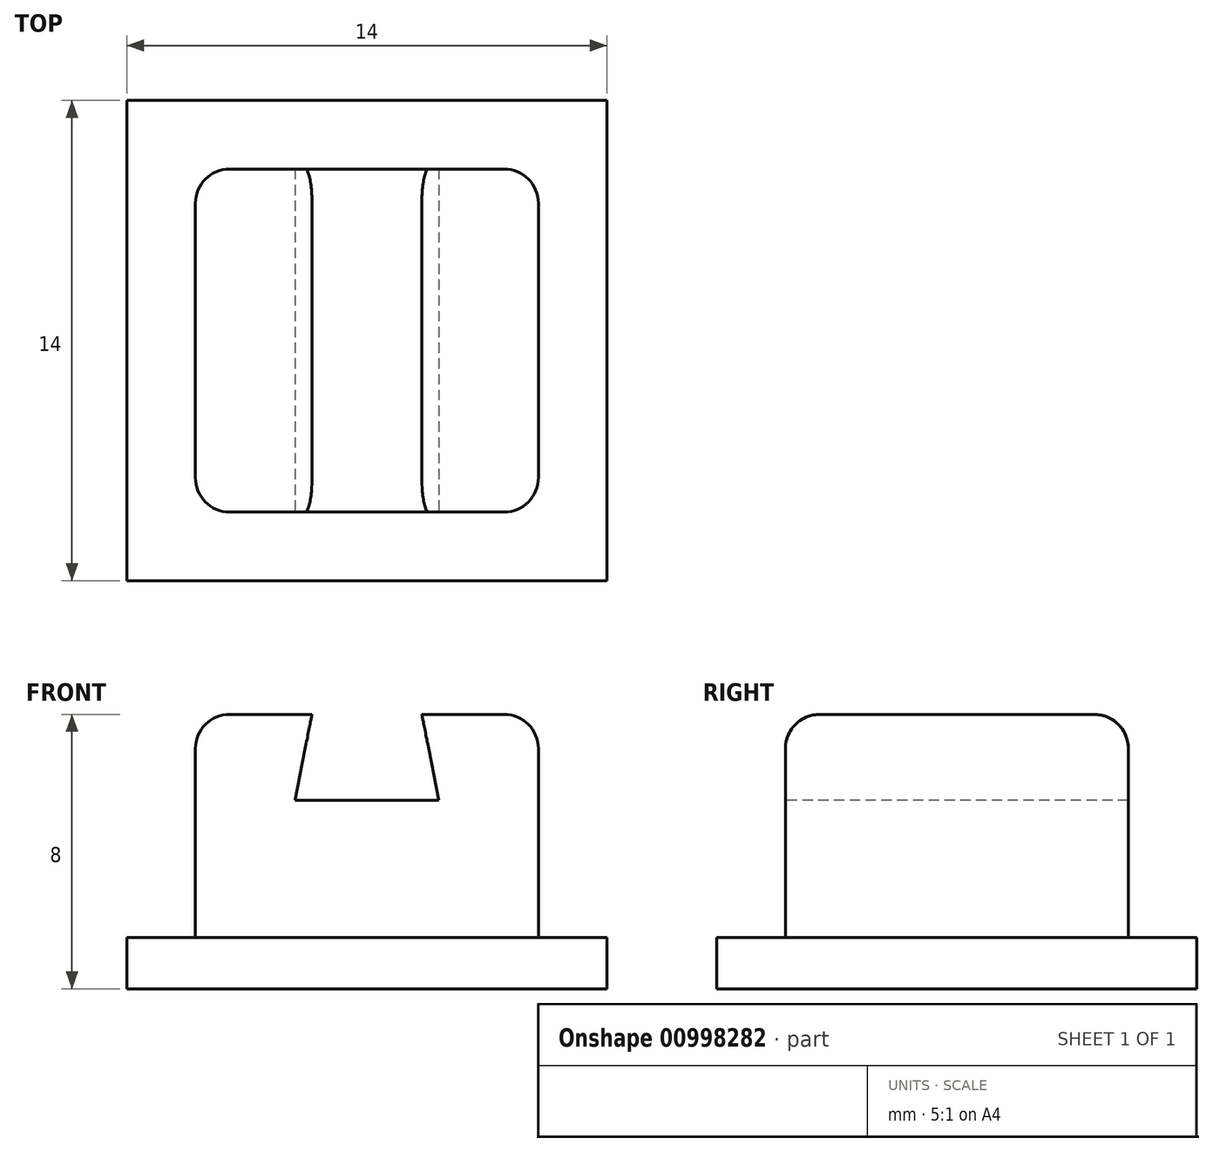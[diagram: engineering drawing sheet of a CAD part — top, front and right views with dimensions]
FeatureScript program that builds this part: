
annotation { "Feature Type Name" : "Feature", "Feature Type Description" : "" }
export const myFeature = defineFeature(function(context is Context, id is Id, definition is map)
    precondition{}
    {
        {
            var Q0;
            Q0=qCreatedBy(makeId("Top.planeOp"),FACE);
            var sketch = newSketch(context, id + "F0", { "sketchPlane" : qUnion([Q0])});
            skLineSegment(sketch, "E0.bottom", {"start": v(7, 7) * mm, "end": v(-7, 7) * mm});
            skLineSegment(sketch, "E0.top", {"start": v(7, -7) * mm, "end": v(-7, -7) * mm});
            skLineSegment(sketch, "E0.left", {"start": v(7, 7) * mm, "end": v(7, -7) * mm});
            skLineSegment(sketch, "E0.right", {"start": v(-7, 7) * mm, "end": v(-7, -7) * mm});
            skPoint(sketch, "E0.middle", {"position": v(0, 0) * mm});
            skLineSegment(sketch, "E1.0", {"start": v(5, 5) * mm, "end": v(-5, 5) * mm});
            skLineSegment(sketch, "E2.0", {"start": v(5, 5) * mm, "end": v(5, -5) * mm});
            skLineSegment(sketch, "E3.0", {"start": v(5, -5) * mm, "end": v(-5, -5) * mm});
            skLineSegment(sketch, "E4.0", {"start": v(-5, 5) * mm, "end": v(-5, -5) * mm});
            skSolve(sketch);
        }
        {
            var Q0;
            Q0=makeQuery(id+"F0.imprint","IMPRINT",FACE,{"disambiguationData":[TD([[makeQuery(id+"F0.imprint","IMPRINT",EDGE,{"derivedFrom":sQuery(id+"F0.wireOp",EDGE,"E0.bottom")}),1.0]])]});
            extrude(context, id + "F1", {"entities" : qUnion([Q0]), "depth" : 1.5 * mm, "offsetDistance" : 25 * mm});
        }
        {
            var Q0;
            Q0=makeQuery(id+"F0.imprint","IMPRINT",FACE,{"disambiguationData":[TD([[makeQuery(id+"F0.imprint","IMPRINT",EDGE,{"derivedFrom":sQuery(id+"F0.wireOp",EDGE,"E1.0")}),1.0]])]});
            extrude(context, id + "F2", {"entities" : qUnion([Q0]), "operationType" : NewBodyOperationType.ADD, "depth" : 8 * mm, "offsetDistance" : 25 * mm});
        }
        {
            var Q0;
            Q0=makeQuery(id+"F2.opExtrude","SWEPT_FACE",FACE,{"disambiguationData":[OSD([sQuery(id+"F0.wireOp",EDGE,"E3.0")])]});
            var sketch = newSketch(context, id + "F3", { "sketchPlane" : qUnion([Q0])});
            skLineSegment(sketch, "E5", {"start": v(-1.6, 8) * mm, "end": v(-1.6, 1.5) * mm, "construction": true});
            skLineSegment(sketch, "E6", {"start": v(1.6, 8) * mm, "end": v(1.6, 1.5) * mm, "construction": true});
            skLineSegment(sketch, "E7", {"start": v(-2.1, 8) * mm, "end": v(-2.1, 1.5) * mm, "construction": true});
            skLineSegment(sketch, "E8", {"start": v(2.1, 8) * mm, "end": v(2.1, 1.5) * mm, "construction": true});
            skPoint(sketch, "E9", {"position": v(2.1, 5.5) * mm});
            skPoint(sketch, "E10", {"position": v(-2.1, 5.5) * mm});
            skLineSegment(sketch, "E11", {"start": v(-1.6, 8) * mm, "end": v(-2.1, 5.5) * mm});
            skLineSegment(sketch, "E12", {"start": v(1.6, 8) * mm, "end": v(2.1, 5.5) * mm});
            skLineSegment(sketch, "E13", {"start": v(-2.1, 5.5) * mm, "end": v(2.1, 5.5) * mm});
            skLineSegment(sketch, "E14", {"start": v(-1.6, 8) * mm, "end": v(1.6, 8) * mm});
            skSolve(sketch);
        }
        {
            var Q0;
            Q0 = qSketchRegion(id + "F3", true);
            extrude(context, id + "F4", {"entities" : qUnion([Q0]), "operationType" : NewBodyOperationType.REMOVE, "oppositeDirection" : true, "depth" : 25 * mm, "offsetDistance" : 25 * mm});
        }
        {
            var Q0;
            Q0=makeQuery(id+"F2.opExtrude","CAP_EDGE",EDGE,{"disambiguationData":[OSD([sQuery(id+"F0.wireOp",EDGE,"E4.0")])],"isStart":false});
            var Q1;
            {var subQ0=sQuery(id+"F0.wireOp",EDGE,"E4.0");var subQ1=sQuery(id+"F0.wireOp",EDGE,"E3.0");Q1=makeQuery(id+"F4.boolean.opBoolean","SPLIT",EDGE,{"disambiguationData":[TD([makeQuery(id+"F2.opExtrude","SWEPT_FACE",FACE,{"disambiguationData":[OSD([subQ0])]})])],"derivedFrom":makeQuery(id+"F2.opExtrude","CAP_EDGE",EDGE,{"disambiguationData":[OSD([subQ1])],"isStart":false})});}
            var Q2;
            {var subQ0=sQuery(id+"F0.wireOp",EDGE,"E3.0");var subQ1=sQuery(id+"F0.wireOp",EDGE,"E2.0");Q2=makeQuery(id+"F4.boolean.opBoolean","SPLIT",EDGE,{"disambiguationData":[TD([makeQuery(id+"F2.opExtrude","SWEPT_FACE",FACE,{"disambiguationData":[OSD([subQ1])]})])],"derivedFrom":makeQuery(id+"F2.opExtrude","CAP_EDGE",EDGE,{"disambiguationData":[OSD([subQ0])],"isStart":false})});}
            var Q3;
            {var subQ0=sQuery(id+"F0.wireOp",EDGE,"E1.0");var subQ1=sQuery(id+"F0.wireOp",EDGE,"E2.0");Q3=makeQuery(id+"F4.boolean.opBoolean","SPLIT",EDGE,{"disambiguationData":[TD([makeQuery(id+"F2.opExtrude","SWEPT_FACE",FACE,{"disambiguationData":[OSD([subQ1])]})])],"derivedFrom":makeQuery(id+"F2.opExtrude","CAP_EDGE",EDGE,{"disambiguationData":[OSD([subQ0])],"isStart":false})});}
            var Q4;
            {var subQ0=sQuery(id+"F0.wireOp",EDGE,"E1.0");var subQ1=sQuery(id+"F0.wireOp",EDGE,"E4.0");Q4=makeQuery(id+"F4.boolean.opBoolean","SPLIT",EDGE,{"disambiguationData":[TD([makeQuery(id+"F2.opExtrude","SWEPT_FACE",FACE,{"disambiguationData":[OSD([subQ1])]})])],"derivedFrom":makeQuery(id+"F2.opExtrude","CAP_EDGE",EDGE,{"disambiguationData":[OSD([subQ0])],"isStart":false})});}
            var Q5;
            Q5=makeQuery(id+"F2.opExtrude","SWEPT_EDGE",EDGE,{"disambiguationData":[OSD([sQuery(id+"F0.wireOp",EDGE,"E1.0"),sQuery(id+"F0.wireOp",EDGE,"E4.0")])]});
            var Q6;
            Q6=makeQuery(id+"F2.opExtrude","SWEPT_EDGE",EDGE,{"disambiguationData":[OSD([sQuery(id+"F0.wireOp",EDGE,"E3.0"),sQuery(id+"F0.wireOp",EDGE,"E4.0")])]});
            var Q7;
            Q7=makeQuery(id+"F2.opExtrude","SWEPT_EDGE",EDGE,{"disambiguationData":[OSD([sQuery(id+"F0.wireOp",EDGE,"E2.0"),sQuery(id+"F0.wireOp",EDGE,"E3.0")])]});
            var Q8;
            Q8=makeQuery(id+"F2.opExtrude","SWEPT_EDGE",EDGE,{"disambiguationData":[OSD([sQuery(id+"F0.wireOp",EDGE,"E1.0"),sQuery(id+"F0.wireOp",EDGE,"E2.0")])]});
            var Q9;
            Q9=makeQuery(id+"F2.opExtrude","CAP_EDGE",EDGE,{"disambiguationData":[OSD([sQuery(id+"F0.wireOp",EDGE,"E2.0")])],"isStart":false});
            fillet(context, id + "F5", {"entities" : qUnion([Q0, Q1, Q2, Q3, Q4, Q5, Q6, Q7, Q8, Q9]), "radius" : 1 * mm, "tangentPropagation" : true, "allowEdgeOverflow" : false});
        }
    });
